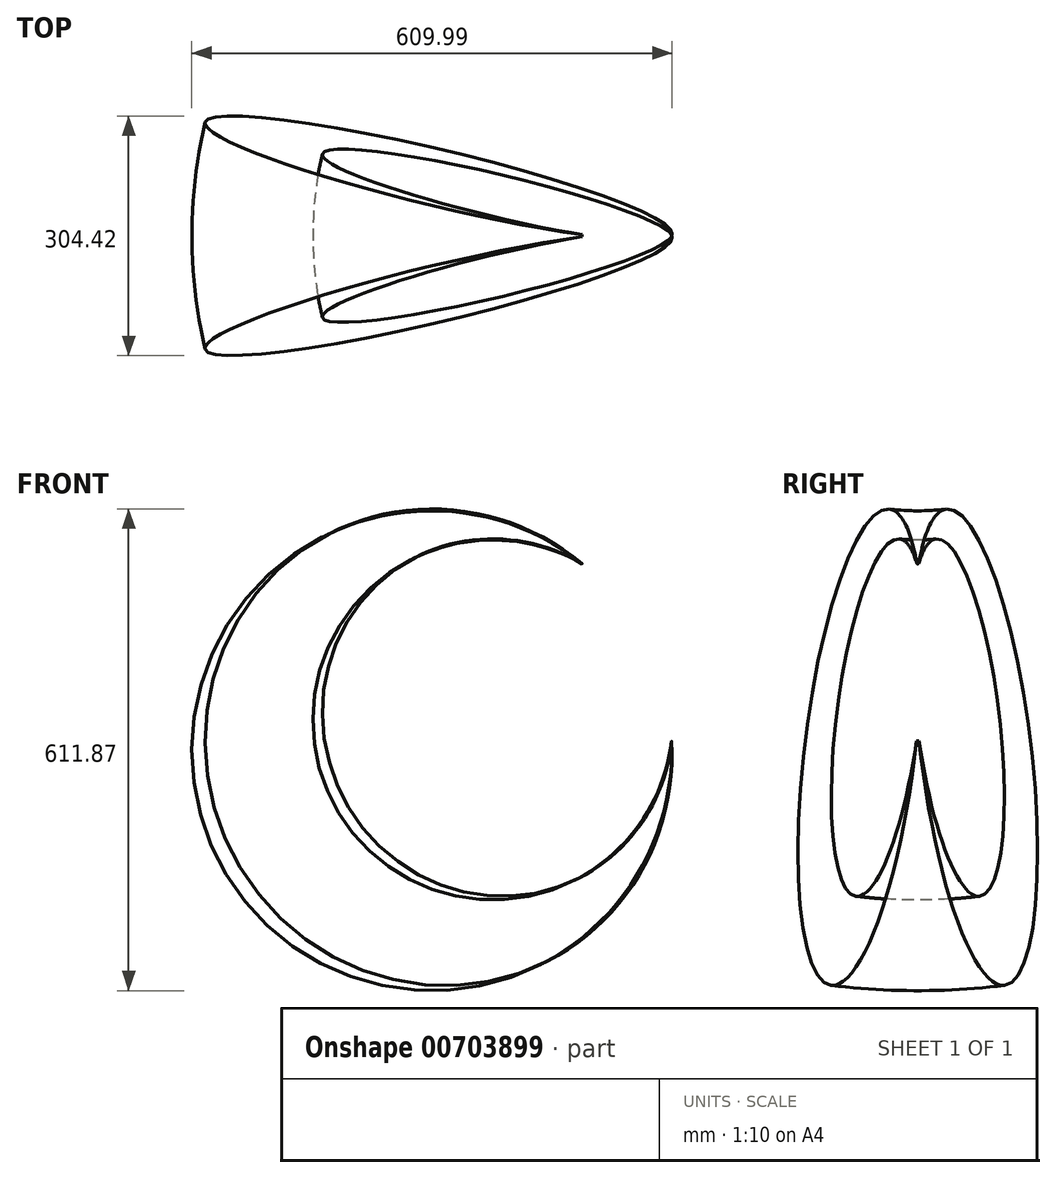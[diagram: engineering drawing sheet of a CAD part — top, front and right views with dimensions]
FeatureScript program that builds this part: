
annotation { "Feature Type Name" : "Feature", "Feature Type Description" : "" }
export const myFeature = defineFeature(function(context is Context, id is Id, definition is map)
    precondition{}
    {
        {
            var Q0;
            Q0=qCreatedBy(makeId("Front.planeOp"),FACE);
            var sketch = newSketch(context, id + "F0", { "sketchPlane" : qUnion([Q0])});
            skArc(sketch, "E0", {"start": v(185.87, 240.56) * mm, "mid": v(-277.28, -134.2) * mm, "end": v(299.45, 15.22) * mm});
            skArc(sketch, "E1", {"start": v(185.87, 240.56) * mm, "mid": v(-131.7, -60.81) * mm, "end": v(299.45, 15.22) * mm});
            skSolve(sketch);
        }
        {
            var Q0;
            Q0=qCreatedBy(makeId("Front.planeOp"),FACE);
            var sketch = newSketch(context, id + "F1", { "sketchPlane" : qUnion([Q0])});
            skLineSegment(sketch, "E2", {"start": v(189.19, 245) * mm, "end": v(304.93, 19.2) * mm});
            skSolve(sketch);
        }
        {
            var Q0;
            Q0=makeQuery(id+"F0.imprint","IMPRINT",FACE,{"disambiguationData":[TD([[makeQuery(id+"F0.imprint","IMPRINT",EDGE,{"derivedFrom":sQuery(id+"F0.wireOp",EDGE,"E0")}),1.0]])]});
            var Q1;
            Q1 = qConstructionFilter(qBodyType(qCreatedBy(id + "F0" ,EDGE), BodyType.WIRE), ConstructionObject.NO);
            var Q2;
            Q2=sQuery(id+"F1.wireOp",EDGE,"E2");
            revolve(context, id + "F2", {"bodyType" : ToolBodyType.SURFACE, "surfaceOperationType" : NewSurfaceOperationType.NEW, "entities" : qUnion([Q0]), "surfaceEntities" : qUnion([Q1]), "axis" : qUnion([Q2]), "revolveType" : RevolveType.SYMMETRIC, "angle" : 30 * degree});
        }
    });
